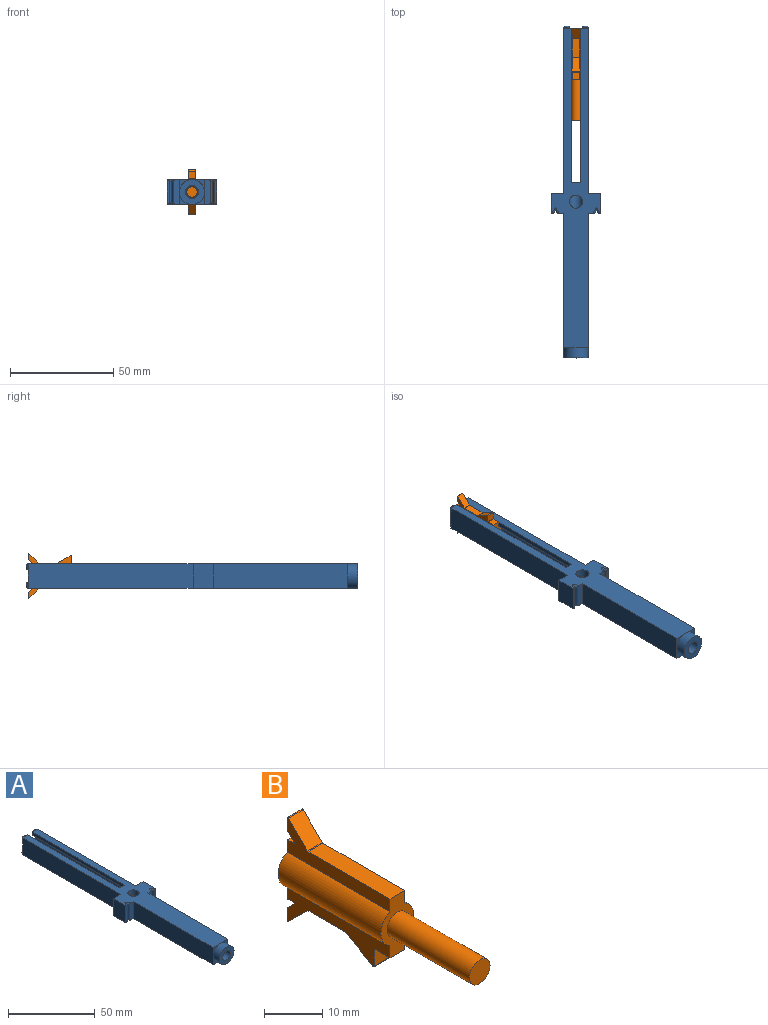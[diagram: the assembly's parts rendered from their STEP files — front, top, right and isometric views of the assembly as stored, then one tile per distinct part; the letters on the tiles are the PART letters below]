
ASSEMBLY  parts=2 mates=1
PART A: 61 faces, bbox 24x161x12 mm
  f0: plane 1.5x1.5mm, normal (0,1,0), area 0.5mm2, adj f16,f44,f55
  f1: plane 1.5x1.5mm, normal (0,1,0), area 0.5mm2, adj f15,f44,f53
  f2: plane 1.5x1.5mm, normal (0,1,0), area 0.5mm2, adj f16,f45,f51
  f3: plane 1.5x1.5mm, normal (0,1,0), area 0.5mm2, adj f15,f45,f49
  f4: plane 75x2.31mm, normal (-1,0,0), area 173mm2, adj f14,f15,f46,f47
  f5: plane 75x2.31mm, normal (1,0,0), area 173mm2, adj f13,f15,f46,f48
  f6: plane 75x2.31mm, normal (-1,0,0), area 173mm2, adj f14,f16,f46,f47
  f7: plane 75x2.31mm, normal (1,0,0), area 173mm2, adj f13,f16,f46,f48
  f8: plane 12x6mm, normal (0,1,0), area 72mm2, adj f15,f16,f22,f45
  f9: plane 12x6mm, normal (0,1,0), area 72mm2, adj f15,f16,f20,f44
  f10: plane 12x3mm, normal (0,-1,0), area 35.7mm2, adj f15,f16,f24,f31,f33,f40
  f11: cylinder r=6mm len=12mm, axis (0,1,0), area 188.5mm2, adj f19,f39,f41,f42,f43
  f12: cylinder r=3.2mm len=79mm, axis (0,1,0), area 1547.4mm2, adj f19,f35,f37
  f13: cylinder r=4.2mm len=75mm, axis (0,-1,0), area 676.9mm2, adj f5,f7,f46,f48
  f14: cylinder r=4.2mm len=75mm, axis (0,-1,0), area 676.9mm2, adj f4,f6,f46,f47
  f15: plane 155x24mm, normal (0,0,1), area 1636.3mm2, adj f1,f3,f4,f5,f8,f9,f10,f17
  f16: plane 155x24mm, normal (0,0,-1), area 1668.5mm2, adj f0,f2,f6,f7,f8,f9,f10,f17
  f17: plane 12x3mm, normal (0,-1,0), area 35.7mm2, adj f15,f16,f26,f27,f29,f38
  f18: plane 12x1mm, normal (0,-1,0), area 11.7mm2, adj f15,f16,f22,f23,f32,f34
  f19: plane 12x12mm, normal (0,-1,0), area 80.9mm2, adj f11,f12
  f20: plane 12x10mm, normal (-1,0,0), area 120mm2, adj f9,f15,f16,f21
  f21: plane 12x1mm, normal (0,-1,0), area 11.7mm2, adj f15,f16,f20,f25,f28,f30
  f22: plane 12x10mm, normal (1,0,0), area 120mm2, adj f8,f15,f16,f18
  f23: plane 10.4x1.5mm, normal (-0.83,-0.55,0), area 18.7mm2, adj f18,f24,f32,f34
  f24: plane 10.4x1.5mm, normal (0.83,-0.55,0), area 18.7mm2, adj f10,f23,f31,f33
  f25: plane 10.4x1.5mm, normal (0.83,-0.55,0), area 18.7mm2, adj f21,f26,f28,f30
  f26: plane 10.4x1.5mm, normal (-0.83,-0.55,0), area 18.7mm2, adj f17,f25,f27,f29
  f27: cylinder r=0.8mm len=3.39mm, axis (0.55,-0.83,0), area 3.1mm2, adj f15,f17,f26,f28
  f28: cylinder r=0.8mm len=3.39mm, axis (0.55,0.83,0), area 3.1mm2, adj f15,f21,f25,f27
  f29: cylinder r=0.8mm len=3.39mm, axis (-0.55,0.83,0), area 3.1mm2, adj f16,f17,f26,f30
  f30: cylinder r=0.8mm len=3.39mm, axis (-0.55,-0.83,0), area 3.1mm2, adj f16,f21,f25,f29
  f31: cylinder r=0.8mm len=3.39mm, axis (0.55,0.83,0), area 3.1mm2, adj f10,f15,f24,f32
  f32: cylinder r=0.8mm len=3.39mm, axis (0.55,-0.83,0), area 3.1mm2, adj f15,f18,f23,f31
  f33: cylinder r=0.8mm len=3.39mm, axis (-0.55,-0.83,0), area 3.1mm2, adj f10,f16,f24,f34
  f34: cylinder r=0.8mm len=3.39mm, axis (-0.55,0.83,0), area 3.1mm2, adj f16,f18,f23,f33
  f35: cylinder r=3.2mm len=6.4mm, axis (0,0,1), area 79.7mm2, adj f12,f15
  f36: cylinder r=2.75mm len=6mm, axis (0,1,0), area 103.7mm2, adj f37,f46
  f37: plane 6.4x6.4mm, normal (0,-1,0), area 8.4mm2, adj f12,f36
  f38: plane 65x12mm, normal (-1,0,0), area 780mm2, adj f15,f16,f17,f39,f42
  f39: plane 6x6mm, normal (0,-1,0), area 7.7mm2, adj f11,f15,f38
  f40: plane 65x12mm, normal (1,0,0), area 780mm2, adj f10,f15,f16,f41,f43
  f41: plane 6x6mm, normal (0,-1,0), area 7.7mm2, adj f11,f15,f40
  f42: plane 6x6mm, normal (0,-1,0), area 7.7mm2, adj f11,f16,f38
  f43: plane 6x6mm, normal (0,-1,0), area 7.7mm2, adj f11,f16,f40
  f44: plane 80x12mm, normal (-1,0,0), area 960mm2, adj f0,f1,f9,f15,f16,f48
  f45: plane 80x12mm, normal (1,0,0), area 960mm2, adj f2,f3,f8,f15,f16,f47
  f46: plane 12x8.4mm, normal (0,1,0), area 47.4mm2, adj f4,f5,f6,f7,f13,f14,f15,f16
  f47: plane 12x4mm, normal (0,1,0), area 21.3mm2, adj f4,f6,f14,f15,f16,f45,f49,f51
  f48: plane 12x4mm, normal (0,1,0), area 21.3mm2, adj f5,f7,f13,f15,f16,f44,f53,f55
  f49: cylinder r=1.5mm len=3mm, axis (0,-1,0), area 4.7mm2, adj f3,f47,f60
  f50: plane 2x2mm, normal (0,1,0), area 3.1mm2, adj f60
  f51: cylinder r=1.5mm len=3mm, axis (0,-1,0), area 4.7mm2, adj f2,f47,f57
  f52: plane 2x2mm, normal (0,1,0), area 3.1mm2, adj f57
  f53: cylinder r=1.5mm len=3mm, axis (0,-1,0), area 4.7mm2, adj f1,f48,f58
  f54: plane 2x2mm, normal (0,1,0), area 3.1mm2, adj f58
  f55: cylinder r=1.5mm len=3mm, axis (0,-1,0), area 4.7mm2, adj f0,f48,f59
  f56: plane 2x2mm, normal (0,1,0), area 3.1mm2, adj f59
  f57: cone r=1.5mm half-angle=45deg, axis (0,-1,0), area 5.6mm2, adj f51,f52
  f58: cone r=1.5mm half-angle=45deg, axis (0,-1,0), area 5.6mm2, adj f53,f54
  f59: cone r=1mm half-angle=45deg, axis (0,-1,0), area 5.6mm2, adj f55,f56
  f60: cone r=1mm half-angle=45deg, axis (0,-1,0), area 5.6mm2, adj f49,f50
PART B: 36 faces, bbox 8x45x21.8 mm
  f0: plane 9.11x3.6mm, normal (0,0,-1), area 32.8mm2, adj f4,f6,f29,f31
  f1: plane 3.6x1.32mm, normal (0,0,-1), area 4.7mm2, adj f4,f6,f30,f35
  f2: plane 3.6x1.32mm, normal (0,0,1), area 4.7mm2, adj f8,f10,f32,f34
  f3: cylinder r=4mm len=25mm, axis (0,1,0), area 220.8mm2, adj f4,f10,f11,f12
  f4: plane 25x7.35mm, normal (-1,0,0), area 90mm2, adj f0,f1,f3,f5,f11,f12,f18,f19
  f5: plane 3.63x3.6mm, normal (0,0,-1), area 13.1mm2, adj f4,f6,f11,f27
  f6: plane 25x7.35mm, normal (1,0,0), area 90mm2, adj f0,f1,f5,f7,f11,f12,f18,f19
  f7: cylinder r=4mm len=25mm, axis (0,1,0), area 220.8mm2, adj f6,f8,f11,f12
  f8: plane 25x7.35mm, normal (1,0,0), area 76.2mm2, adj f2,f7,f9,f11,f12,f15,f16,f17
  f9: plane 19.92x3.6mm, normal (0,0,1), area 71.7mm2, adj f8,f10,f11,f33
  f10: plane 25x7.35mm, normal (-1,0,0), area 76.2mm2, adj f2,f3,f9,f11,f12,f15,f16,f17
  f11: plane 12.4x8mm, normal (0,-1,0), area 47.5mm2, adj f3,f4,f5,f6,f7,f8,f9,f10
  f12: plane 12x8mm, normal (0,1,0), area 65.7mm2, adj f3,f4,f6,f7,f8,f10,f34,f35
  f13: cylinder r=2.5mm len=20mm, axis (0,1,0), area 314.2mm2, adj f11,f14
  f14: plane 5x5mm, normal (0,-1,0), area 19.6mm2, adj f13
  f15: plane 3.6x1.6mm, normal (0,0.71,-0.71), area 8.1mm2, adj f8,f10,f23,f32
  f16: plane 3.6x2.43mm, normal (0,1,0), area 8.8mm2, adj f8,f10,f23,f24
  f17: plane 4.6x4.6mm, normal (0,-0.71,0.71), area 23.4mm2, adj f8,f10,f24,f33
  f18: plane 4.6x4.6mm, normal (0,-0.71,-0.71), area 23.4mm2, adj f4,f6,f21,f31
  f19: plane 3.6x2.43mm, normal (0,1,0), area 8.8mm2, adj f4,f6,f21,f22
  f20: plane 3.6x1.6mm, normal (0,0.71,0.71), area 8.1mm2, adj f4,f6,f22,f30
  f21: cylinder r=0.2mm len=3.6mm, axis (-1,0,0), area 1.7mm2, adj f4,f6,f18,f19
  f22: cylinder r=0.2mm len=3.6mm, axis (-1,0,0), area 0.6mm2, adj f4,f6,f19,f20
  f23: cylinder r=0.2mm len=3.6mm, axis (-1,0,0), area 0.6mm2, adj f8,f10,f15,f16
  f24: cylinder r=0.2mm len=3.6mm, axis (-1,0,0), area 1.7mm2, adj f8,f10,f16,f17
  f25: plane 3.6x3.45mm, normal (0,-1,0), area 12.4mm2, adj f4,f6,f27,f28
  f26: plane 6.58x3.8mm, normal (0,0.5,-0.87), area 27.4mm2, adj f4,f6,f28,f29
  f27: cylinder r=0.2mm len=3.6mm, axis (1,0,0), area 1.1mm2, adj f4,f5,f6,f25
  f28: cylinder r=0.2mm len=3.6mm, axis (1,0,0), area 1.5mm2, adj f4,f6,f25,f26
  f29: cylinder r=0.2mm len=3.6mm, axis (1,0,0), area 0.4mm2, adj f0,f4,f6,f26
  f30: cylinder r=0.2mm len=3.6mm, axis (-1,0,0), area 1.7mm2, adj f1,f4,f6,f20
  f31: cylinder r=0.2mm len=3.6mm, axis (-1,0,0), area 0.6mm2, adj f0,f4,f6,f18
  f32: cylinder r=0.2mm len=3.6mm, axis (-1,0,0), area 1.7mm2, adj f2,f8,f10,f15
  f33: cylinder r=0.2mm len=3.6mm, axis (-1,0,0), area 0.6mm2, adj f8,f9,f10,f17
  f34: cylinder r=0.2mm len=3.6mm, axis (-1,0,0), area 1.1mm2, adj f2,f8,f10,f12
  f35: cylinder r=0.2mm len=3.6mm, axis (1,0,0), area 1.1mm2, adj f1,f4,f6,f12
PLACE A t=(-6.04,31.21,-4.57)mm
PLACE B rot(axis=(0,1,0),180deg) t=(-6.04,111.21,-4.57)mm
MATE slider B.f13 <-> A.f36  axis (0,1,0) through (-6.04,76.21,-4.57)mm
